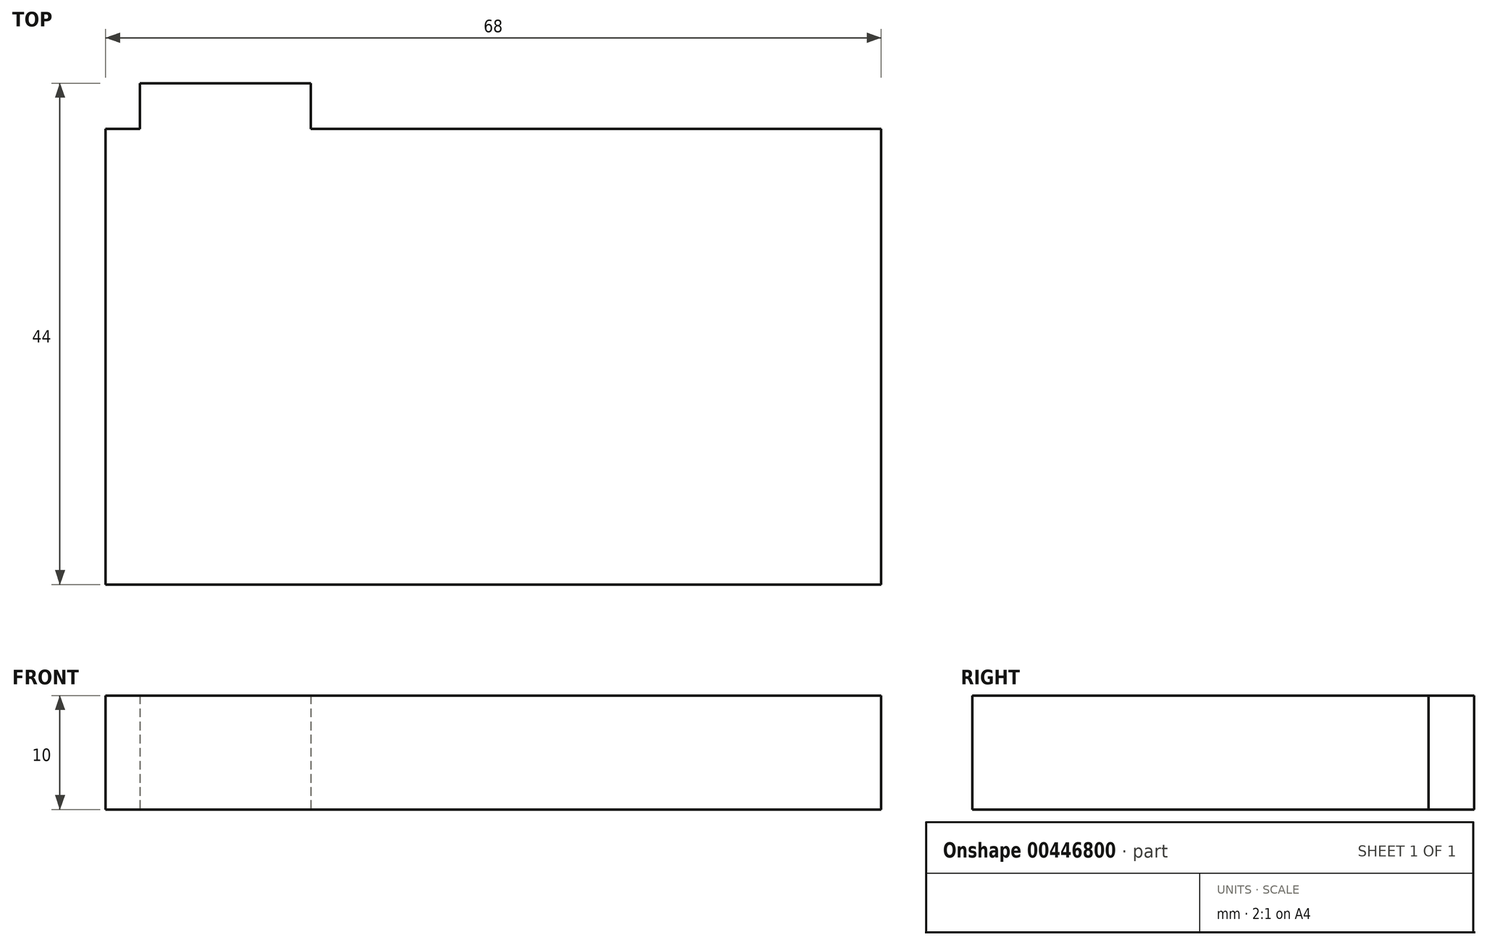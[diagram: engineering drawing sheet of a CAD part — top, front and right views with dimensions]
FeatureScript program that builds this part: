
annotation { "Feature Type Name" : "Feature", "Feature Type Description" : "" }
export const myFeature = defineFeature(function(context is Context, id is Id, definition is map)
    precondition{}
    {
        {
            var Q0;
            Q0=qCreatedBy(makeId("Front.planeOp"),FACE);
            var sketch = newSketch(context, id + "F0", { "sketchPlane" : qUnion([Q0])});
            skLineSegment(sketch, "E0.bottom", {"start": v(-34, 5) * mm, "end": v(34, 5) * mm});
            skLineSegment(sketch, "E0.top", {"start": v(-34, -5) * mm, "end": v(34, -5) * mm});
            skLineSegment(sketch, "E0.left", {"start": v(-34, 5) * mm, "end": v(-34, -5) * mm});
            skLineSegment(sketch, "E0.right", {"start": v(34, 5) * mm, "end": v(34, -5) * mm});
            skSolve(sketch);
        }
        {
            var Q0;
            Q0=qSketchRegion(id+"F0",true);
            extrude(context, id + "F1", {"entities" : qUnion([Q0]), "depth" : 40 * mm});
        }
        {
            var Q0;
            Q0=makeQuery(id+"F1.opExtrude","CAP_FACE",FACE,{"disambiguationData":[OSD([sQuery(id+"F0.wireOp",EDGE,"E0.bottom"),sQuery(id+"F0.wireOp",EDGE,"E0.top"),sQuery(id+"F0.wireOp",EDGE,"E0.left"),sQuery(id+"F0.wireOp",EDGE,"E0.right")])],"isStart":true});
            var sketch = newSketch(context, id + "F2", { "sketchPlane" : qUnion([Q0])});
            skLineSegment(sketch, "E1.bottom", {"start": v(16, 5) * mm, "end": v(31, 5) * mm});
            skLineSegment(sketch, "E1.top", {"start": v(16, -5) * mm, "end": v(31, -5) * mm});
            skLineSegment(sketch, "E1.left", {"start": v(16, 5) * mm, "end": v(16, -5) * mm});
            skLineSegment(sketch, "E1.right", {"start": v(31, 5) * mm, "end": v(31, -5) * mm});
            skSolve(sketch);
        }
        {
            var Q0;
            Q0=qSketchRegion(id+"F2",true);
            extrude(context, id + "F3", {"entities" : qUnion([Q0]), "operationType" : NewBodyOperationType.ADD, "depth" : 4 * mm});
        }
    });
